# Revit family: Storage-Freestanding-Teknion-RBTPS_Mobile_Pedestal_with_Seat-R2019
name_source: partatom
category: Furniture
units: mm (PartAtom-declared; Revit-internal decimal feet)

## family parameters
Always vertical = Yes
Cut with Voids When Loaded = No
OmniClass Number = 23.40.20.00
OmniClass Title = General Furniture and Specialties
Room Calculation Point = No
Shared = Yes
Work Plane-Based = No

## types (1)
- 18" Depth, Box, File
    Assembly Code = E2020200
    Description = Mobile Pedestal with Seat, 18" Depth, Box, File Drawer Configuration
    Manufacturer = Teknion
    Manufacturer Fax = 416.661.4586
    Model = RBTPS180612
    Part Number = RBTPS
    Product Documentation Link = https://www.teknion.com
    Product Line = Expansion Desking
    Product Page URL = https://www.teknion.com
    Series = Expansion Desking
    Sustainability Data = http://www.teknion.com
    URL = www.teknion.com
    Unit Weight URL = http://www.teknion.com
    Warranty = http://www.teknion.com

## geometry (parser evidence)
native form markers: Sweep x1
no freeform markers — native parametric forms only
